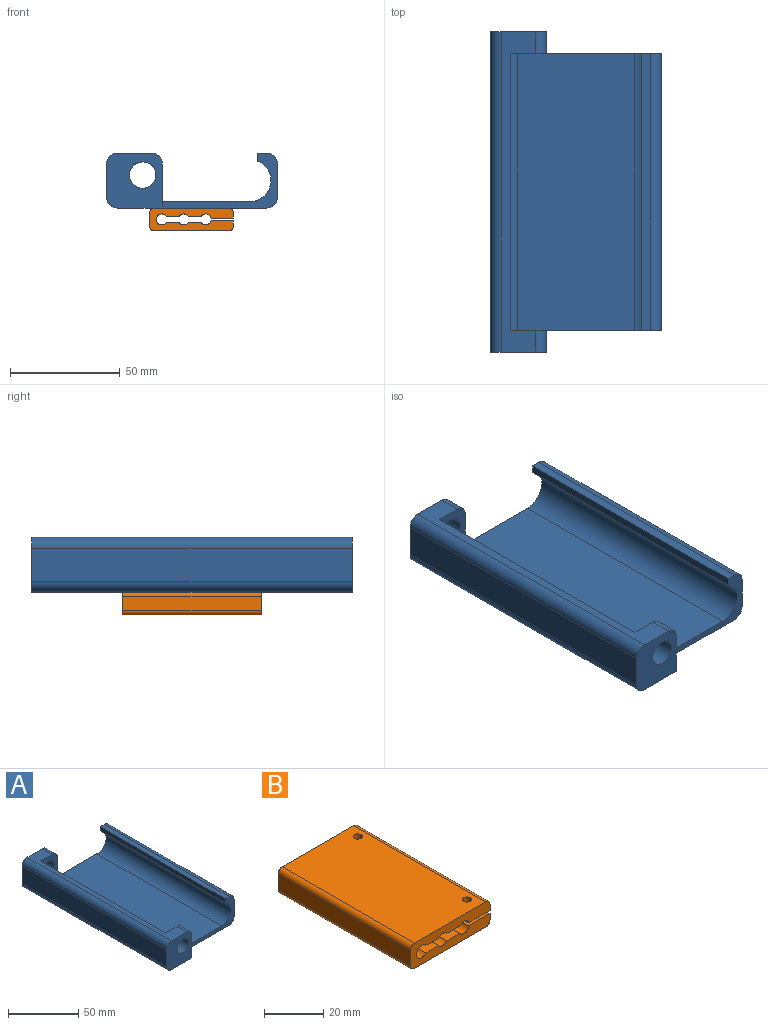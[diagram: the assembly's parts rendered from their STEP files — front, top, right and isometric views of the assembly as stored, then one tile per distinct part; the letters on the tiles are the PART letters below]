
ASSEMBLY  parts=2 mates=1
PART A: 26 faces, bbox 78x146x25 mm
  f0: plane 52.5x25mm, normal (0,1,0), area 268.7mm2, adj f4,f5,f6,f7,f8,f9,f16,f24
  f1: plane 52.5x25mm, normal (0,-1,0), area 268.7mm2, adj f4,f5,f6,f7,f8,f9,f12,f24
  f2: plane 146x15.5mm, normal (0,0,1), area 814mm2, adj f11,f14,f15,f18,f19,f20,f21,f22
  f3: plane 146x15mm, normal (-1,0,0), area 2190mm2, adj f14,f18,f22,f23
  f4: plane 146x68mm, normal (0,0,-1), area 8978mm2, adj f0,f1,f12,f14,f16,f18,f23,f24
  f5: plane 126x15mm, normal (1,0,0), area 1890mm2, adj f0,f1,f24,f25
  f6: plane 126x4mm, normal (0,0,1), area 504mm2, adj f0,f1,f7,f25
  f7: plane 126x3.67mm, normal (-1,0,0), area 462.2mm2, adj f0,f1,f6,f8
  f8: cylinder r=9.5mm len=126mm, axis (0,1,0), area 3308.8mm2, adj f0,f1,f7,f9
  f9: plane 126x53mm, normal (0,0,1), area 6678mm2, adj f0,f1,f8,f10,f15,f19
  f10: cylinder r=9.5mm len=126mm, axis (0,1,0), area 3308.8mm2, adj f9,f11,f15,f19
  f11: plane 126x3.67mm, normal (1,0,0), area 462.2mm2, adj f2,f10,f15,f19
  f12: plane 20x10mm, normal (1,0,0), area 200mm2, adj f1,f4,f14,f15,f21
  f13: cylinder r=6mm len=12mm, axis (0,1,0), area 377mm2, adj f14,f15
  f14: plane 25.5x25mm, normal (0,-1,0), area 508.3mm2, adj f2,f3,f4,f12,f13,f21,f22,f23
  f15: plane 22.5x22mm, normal (0,1,0), area 320.6mm2, adj f2,f9,f10,f11,f12,f13,f21
  f16: plane 20x10mm, normal (1,0,0), area 200mm2, adj f0,f4,f18,f19,f20
  f17: cylinder r=6mm len=12mm, axis (0,-1,0), area 377mm2, adj f18,f19
  f18: plane 25.5x25mm, normal (0,1,0), area 508.3mm2, adj f2,f3,f4,f16,f17,f20,f22,f23
  f19: plane 22.5x22mm, normal (0,-1,0), area 320.6mm2, adj f2,f9,f10,f11,f16,f17,f20
  f20: cylinder r=5mm len=10mm, axis (0,1,0), area 78.5mm2, adj f2,f16,f18,f19
  f21: cylinder r=5mm len=10mm, axis (0,1,0), area 78.5mm2, adj f2,f12,f14,f15
  f22: cylinder r=5mm len=146mm, axis (0,-1,0), area 1146.7mm2, adj f2,f3,f14,f18
  f23: cylinder r=5mm len=146mm, axis (0,1,0), area 1146.7mm2, adj f3,f4,f14,f18
  f24: cylinder r=5mm len=126mm, axis (0,-1,0), area 989.6mm2, adj f0,f1,f4,f5
  f25: cylinder r=5mm len=126mm, axis (0,1,0), area 989.6mm2, adj f0,f1,f5,f6
PART B: 26 faces, bbox 38x63x10.4 mm
  f0: plane 63x2.61mm, normal (1,0,0), area 164.2mm2, adj f1,f16,f17,f23
  f1: plane 63x10.07mm, normal (0,0,1), area 595.3mm2, adj f0,f2,f16,f17,f18,f19
  f2: cylinder r=2.5mm len=63mm, axis (0,1,0), area 355.3mm2, adj f1,f3,f16,f17
  f3: plane 63x6mm, normal (0,0,1), area 378mm2, adj f2,f4,f16,f17
  f4: cylinder r=2.5mm len=63mm, axis (0,1,0), area 292.1mm2, adj f3,f5,f16,f17
  f5: plane 63x6mm, normal (0,0,1), area 378mm2, adj f4,f6,f16,f17
  f6: cylinder r=2.5mm len=63mm, axis (0,1,0), area 786.9mm2, adj f5,f7,f16,f17
  f7: plane 63x6mm, normal (0,0,-1), area 378mm2, adj f6,f8,f16,f17
  f8: cylinder r=2.5mm len=63mm, axis (0,1,0), area 292.1mm2, adj f7,f9,f16,f17
  f9: plane 63x6mm, normal (0,0,-1), area 378mm2, adj f8,f10,f16,f17
  f10: cylinder r=2.5mm len=63mm, axis (0,1,0), area 355.3mm2, adj f9,f11,f16,f17
  f11: plane 63x10.07mm, normal (0,0,-1), area 620.5mm2, adj f10,f12,f16,f17,f24,f25
  f12: plane 63x2.61mm, normal (1,0,0), area 164.2mm2, adj f11,f16,f17,f20
  f13: plane 63x34mm, normal (0,0,1), area 2127.9mm2, adj f16,f17,f20,f21,f24,f25
  f14: plane 63x6.41mm, normal (-1,0,0), area 404.1mm2, adj f16,f17,f21,f22
  f15: plane 63x34mm, normal (0,0,-1), area 2102.7mm2, adj f16,f17,f18,f19,f22,f23
  f16: plane 38x10.41mm, normal (0,-1,0), area 289.5mm2, adj f0,f1,f2,f3,f4,f5,f6,f7
  f17: plane 38x10.41mm, normal (0,1,0), area 289.5mm2, adj f0,f1,f2,f3,f4,f5,f6,f7
  f18: cylinder r=2.5mm len=5mm, axis (0,0,-1), area 72.4mm2, adj f1,f15
  f19: cylinder r=2.5mm len=5mm, axis (0,0,-1), area 72.4mm2, adj f1,f15
  f20: cylinder r=2mm len=63mm, axis (0,1,0), area 197.9mm2, adj f12,f13,f16,f17
  f21: cylinder r=2mm len=63mm, axis (0,-1,0), area 197.9mm2, adj f13,f14,f16,f17
  f22: cylinder r=2mm len=63mm, axis (0,1,0), area 197.9mm2, adj f14,f15,f16,f17
  f23: cylinder r=2mm len=63mm, axis (0,-1,0), area 197.9mm2, adj f0,f15,f16,f17
  f24: cylinder r=1.5mm len=4.61mm, axis (0,0,-1), area 43.4mm2, adj f11,f13
  f25: cylinder r=1.5mm len=4.61mm, axis (0,0,-1), area 43.4mm2, adj f11,f13
PLACE A t=(-42.86,-77.47,-82.87)mm
PLACE B t=(-43.09,-108.97,-76.01)mm
MATE planar A.f4 <-> B.f13  axis (0,0,-1) through (-43.95,-140.47,-95.37)mm
